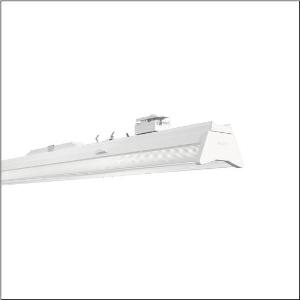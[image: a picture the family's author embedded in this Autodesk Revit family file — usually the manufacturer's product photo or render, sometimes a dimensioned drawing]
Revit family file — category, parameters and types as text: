
# Revit family: licross_r__11_performance_ho_51td16cn4exm_ed55
name_source: partatom
category: Lighting Fixtures
units: mm (PartAtom-declared; Revit-internal decimal feet)

## family parameters
Cut with Voids When Loaded = No
Host = Face
Light Source = No
Part Type = Normal
Room Calculation Point = No
Round Connector Dimension = Use Diameter
Shared = No

## types (1)
- --- (1 x LED, 14420 lm, 77.6 W, 4000K)
    Apparent Load = 78 VA
    CIE Flux Codes = 63 87 95 78 100
    Color Rendering = 80
    Color Temperature = 4000K
    Default Elevation = 1800 mm
    Description = Licross® 11 Performance HO, luminaire insert, of sheet steel, galvanised, coil coated, white, length: 1.500mm, width: 120mm, height: 123mm, LED rated luminous flux: 14.420lm, light colour: 840, control gear: ON/OFF Multilumen, CLOi, with plug, 3-pole, with phase selection, mains connection: 220..240V, AC, 50/60Hz, start of lifetime: 78W, end of service life: 87W, halogen-free wiring, primary light control with lens, of plastic, primary optical cover: cover, of PMMA, light emission: direct/indirect distribution, primary light characteristic: symmetric, protection rating (complete): IP54, insulation class (complete): insulation class I (protective earthing), certification: CE, ENEC, VDE, UKCA, protection symbol: D if used in an environment with non-conductive dust loads with corresponding accessories, impact resistance: IK06, permissible ambient temperature for indoor applications: -35..+35°C, corresponds to IFS (International Featured Standards) requirements for safety and quality in the food industry, reducing of maximum allowable ambient temperature of 5°C with ceiling mounting, LABS conformity tested according to VDMA 24364:2018-05, packaging unit: 1 piece
    Height = 114 mm
    Lamp = 1 x LED
    Lamp Light Flux = 14420 lm
    Lamp Power = 77.6 W
    Lamp count = 1
    Length = 1500 mm
    Luminous efficacy = 186 lm/W
    Manufacturer = Siteco
    ModVariant = No
    Model = 51TD16CN4EXM
    Mounting Place = Ceiling
    Mounting Type = Pendant
    Number of Poles = 1
    OnlyDefault = Yes
    Power Factor = 1
    Product Name = Licross® 11 Performance HO
    Product group = luminaire insert
    ProductGroupID = 901
    Protection Class = Protection class I
    Protection Degree = IP 54
    RLX_Detail_Level = 1
    RLX_Emergency_Light_Flux = 0 lm
    RLX_Emergency_Type = 0
    RLX_Emergency_Type_DB = No
    RlxData = <blob elided: 31901 chars, md5=e190f394>
    Socket = socket
    Standby Power = 0 W
    System Light Flux = 14420 lm
    System Power = 78 W
    Type Comments = factory setting: luminous flux: 100 % | (A | C | E) | 181 mA
    Type Image = l_1256138.jpg
    URL = http://relux.com
    VarID = @adj_038339
    Voltage = 0 V
    Weight = 0.00 kg
    Width = 120 mm

## geometry (parser evidence)
native form markers: Blend x4, Sweep x12
no freeform markers — native parametric forms only
